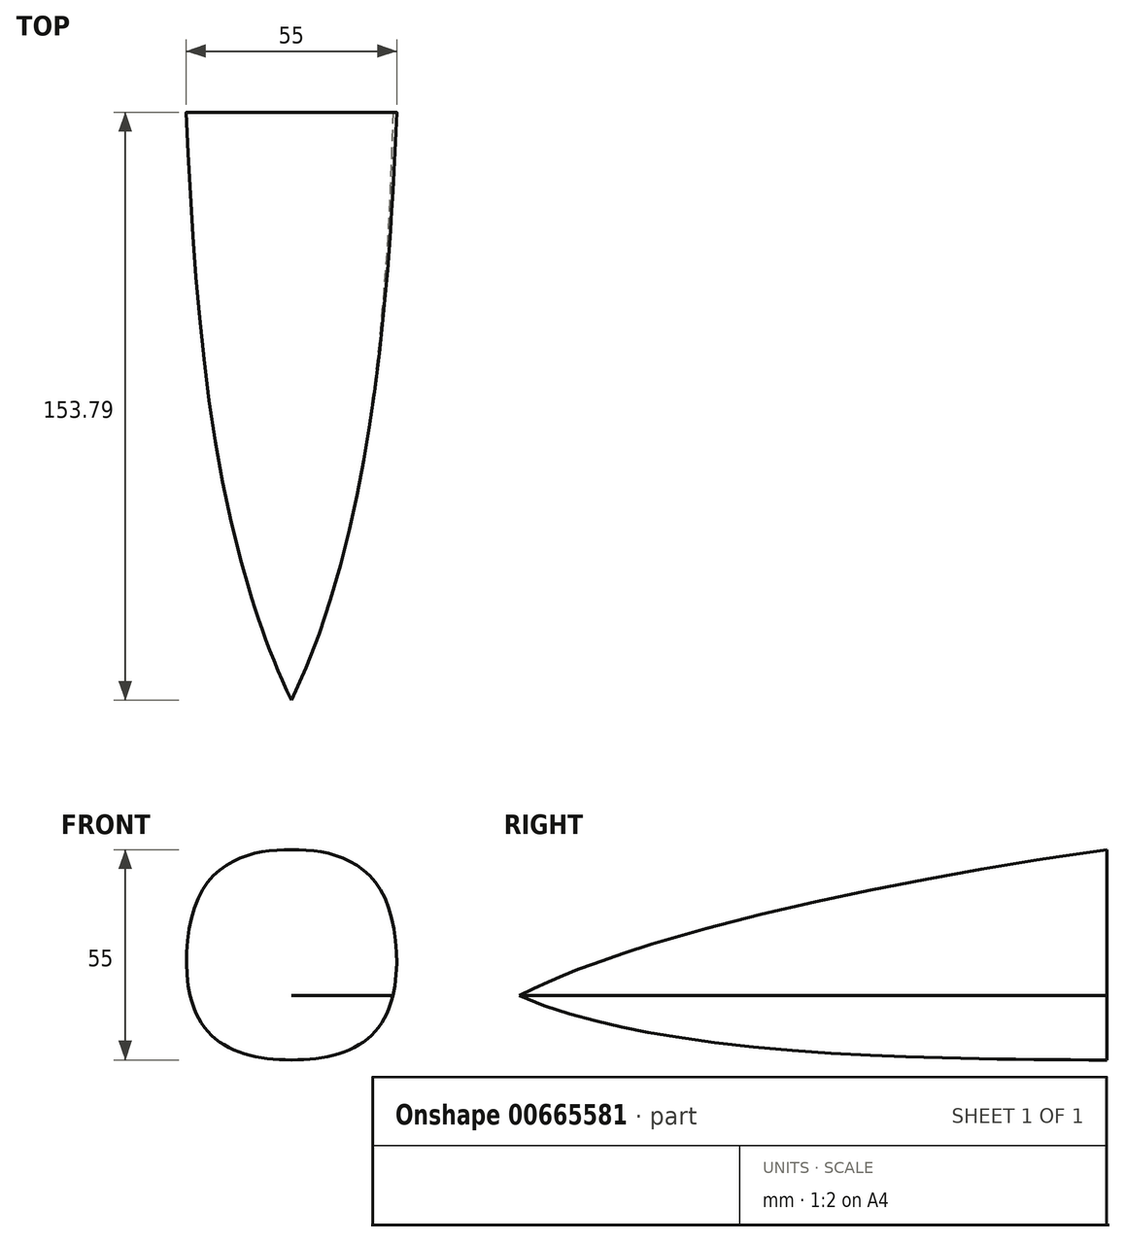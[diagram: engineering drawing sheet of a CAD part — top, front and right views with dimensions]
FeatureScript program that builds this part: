
annotation { "Feature Type Name" : "Feature", "Feature Type Description" : "" }
export const myFeature = defineFeature(function(context is Context, id is Id, definition is map)
    precondition{}
    {
        {
            var Q0;
            Q0=qCreatedBy(makeId("Front.planeOp"),FACE);
            var sketch = newSketch(context, id + "F0", { "sketchPlane" : qUnion([Q0])});
            skPoint(sketch, "E0", {"position": v(26.5, 0) * mm});
            skPoint(sketch, "E1", {"position": v(-26.5, 0) * mm});
            skPoint(sketch, "E2", {"position": v(12.4, 36.39) * mm});
            skPoint(sketch, "E3", {"position": v(-12.4, 36.39) * mm});
            skFitSpline(sketch, "E4", {"points": [v(0, 38.22) * mm, v(12.4, 36.39) * mm, v(24, 26.42) * mm, v(26.5, 0) * mm, v(17.5, -12.91) * mm, v(0, -16.78) * mm, v(-17.5, -12.91) * mm, v(-26.5, 0) * mm, v(-24, 26.42) * mm, v(-12.4, 36.39) * mm, v(0, 38.22) * mm]});
            skPoint(sketch, "E5", {"position": v(0, 26.42) * mm});
            skPoint(sketch, "E6", {"position": v(-27.5, 9.83) * mm});
            skPoint(sketch, "E7", {"position": v(27.5, 9.83) * mm});
            skPoint(sketch, "E8", {"position": v(0, 9.83) * mm});
            skPoint(sketch, "E9", {"position": v(0, -12.91) * mm});
            skSolve(sketch);
        }
        {
            var Q0;
            Q0=qCreatedBy(makeId("Right.planeOp"),FACE);
            var sketch = newSketch(context, id + "F1", { "sketchPlane" : qUnion([Q0])});
            skFitSpline(sketch, "E10", {"points": [v(-153.79, 0) * mm, v(0, 38.22) * mm], "startDerivative": vector(89.32, 46.7) * mm, "endDerivative": vector(179.43, 24.98) * mm});
            skFitSpline(sketch, "E11", {"points": [v(-153.79, 0) * mm, v(0, -16.78) * mm], "startDerivative": vector(106.67, -45.86) * mm, "endDerivative": vector(169.37, -0.4) * mm});
            skSolve(sketch);
        }
        {
            var Q0;
            Q0=qCreatedBy(makeId("Top.planeOp"),FACE);
            var sketch = newSketch(context, id + "F2", { "sketchPlane" : qUnion([Q0])});
            skLineSegment(sketch, "E12.bottom", {"start": v(26.5, 0) * mm, "end": v(-26.5, 0) * mm});
            skLineSegment(sketch, "E12.top", {"start": v(26.5, 51.88) * mm, "end": v(-26.5, 51.88) * mm});
            skLineSegment(sketch, "E12.left", {"start": v(26.5, 0) * mm, "end": v(26.5, 51.88) * mm});
            skLineSegment(sketch, "E12.right", {"start": v(-26.5, 0) * mm, "end": v(-26.5, 51.88) * mm});
            skFitSpline(sketch, "E13", {"points": [v(-26.5, 0) * mm, v(0, -153.79) * mm], "startDerivative": vector(4.13, -147.7) * mm, "endDerivative": vector(64.6, -135.57) * mm});
            skFitSpline(sketch, "E14", {"points": [v(0, -153.79) * mm, v(26.5, 0) * mm], "startDerivative": vector(62.94, 131.65) * mm, "endDerivative": vector(3.8, 144.43) * mm});
            skSolve(sketch);
        }
        {
            var Q0;
            Q0=makeQuery(id+"F0.imprint","IMPRINT",FACE,{"disambiguationData":[TD([[makeQuery(id+"F0.imprint","IMPRINT",EDGE,{"derivedFrom":sQuery(id+"F0.wireOp",EDGE,"E4")}),-1.0]])]});
            var Q1;
            Q1=sQuery(id+"F1.wireOp",VERTEX,"E11.0.internal");
            var Q2;
            Q2=sQuery(id+"F1.wireOp",EDGE,"E10");
            var Q3;
            Q3=sQuery(id+"F1.wireOp",EDGE,"E11");
            var Q4;
            Q4=sQuery(id+"F2.wireOp",EDGE,"E14");
            var Q5;
            Q5=sQuery(id+"F2.wireOp",EDGE,"E13");
            loft(context, id + "F3", {"addGuides" : true, "sheetProfilesArray" : [{ "sheetProfileEntities" : qUnion([Q0]) }, { "sheetProfileEntities" : qUnion([Q1]) }], "guidesArray" : [{ "guideEntities" : qUnion([Q2]), "guideDerivativeType" : LoftGuideDerivativeType.DEFAULT, "guideDerivativeMagnitude" : 1 }, { "guideEntities" : qUnion([Q3]), "guideDerivativeType" : LoftGuideDerivativeType.DEFAULT, "guideDerivativeMagnitude" : 1 }, { "guideEntities" : qUnion([Q4]), "guideDerivativeType" : LoftGuideDerivativeType.DEFAULT, "guideDerivativeMagnitude" : 1 }, { "guideEntities" : qUnion([Q5]), "guideDerivativeType" : LoftGuideDerivativeType.DEFAULT, "guideDerivativeMagnitude" : 1 }]});
        }
    });
